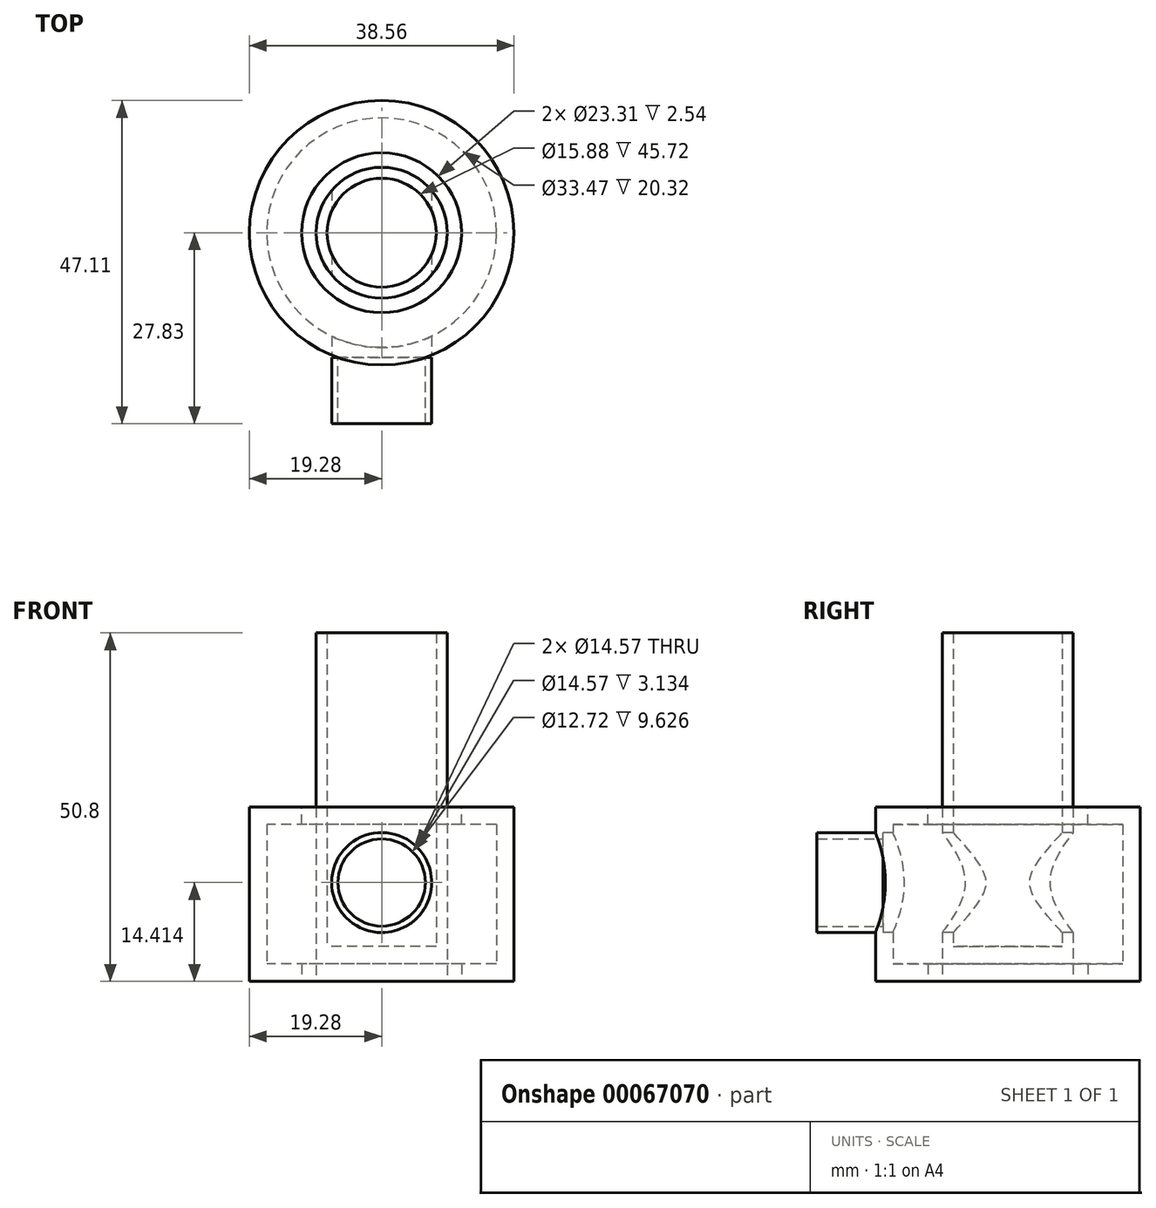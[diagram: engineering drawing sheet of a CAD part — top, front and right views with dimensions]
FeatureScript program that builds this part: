
annotation { "Feature Type Name" : "Feature", "Feature Type Description" : "" }
export const myFeature = defineFeature(function(context is Context, id is Id, definition is map)
    precondition{}
    {
        {
            var Q0;
            Q0=qCreatedBy(makeId("Top.planeOp"),FACE);
            var sketch = newSketch(context, id + "F0", { "sketchPlane" : qUnion([Q0])});
            skCircle(sketch, "E0", {"center": v(0, 0) * mm, "radius": 16.74 * mm});
            skCircle(sketch, "E1", {"center": v(0, 0) * mm, "radius": 11.66 * mm});
            skCircle(sketch, "E2", {"center": v(0, 0) * mm, "radius": 9.54 * mm});
            skCircle(sketch, "E3.0", {"center": v(0, 0) * mm, "radius": 19.28 * mm});
            skCircle(sketch, "E4", {"center": v(0, 0) * mm, "radius": 7.94 * mm});
            skSolve(sketch);
        }
        {
            var Q0;
            Q0=makeQuery(id+"F0.imprint","IMPRINT",FACE,{"disambiguationData":[TD([[makeQuery(id+"F0.imprint","IMPRINT",EDGE,{"derivedFrom":sQuery(id+"F0.wireOp",EDGE,"E0")}),1.0]])]});
            extrude(context, id + "F1", {"entities" : qUnion([Q0]), "depth" : 2.54 * mm});
        }
        {
            var Q0;
            Q0 = qSketchRegion(id + "F0", true);
            extrude(context, id + "F2", {"entities" : qUnion([Q0]), "operationType" : NewBodyOperationType.ADD, "depth" : 25.4 * mm});
        }
        {
            var Q0;
            Q0=makeQuery(id+"F0.imprint","IMPRINT",FACE,{"disambiguationData":[TD([[makeQuery(id+"F0.imprint","IMPRINT",EDGE,{"derivedFrom":sQuery(id+"F0.wireOp",EDGE,"E2")}),1.0]])]});
            extrude(context, id + "F3", {"entities" : qUnion([Q0]), "depth" : 50.8 * mm});
        }
        {
            var Q0;
            Q0=qCreatedBy(makeId("Front.planeOp"),FACE);
            var sketch = newSketch(context, id + "F4", { "sketchPlane" : qUnion([Q0])});
            skCircle(sketch, "E5", {"center": v(0, 14.41) * mm, "radius": 7.29 * mm});
            skSolve(sketch);
        }
        {
            var Q0;
            Q0 = qSketchRegion(id + "F4", true);
            extrude(context, id + "F5", {"entities" : qUnion([Q0]), "operationType" : NewBodyOperationType.REMOVE, "oppositeDirection" : true, "depth" : 11.8 * mm, "hasSecondDirection" : true, "secondDirectionOppositeDirection" : false, "secondDirectionDepth" : 25.05 * mm});
        }
        {
            var Q0;
            Q0=makeQuery(id+"F0.imprint","IMPRINT",FACE,{"disambiguationData":[TD([[makeQuery(id+"F0.imprint","IMPRINT",EDGE,{"derivedFrom":sQuery(id+"F0.wireOp",EDGE,"E4")}),1.0]])]});
            extrude(context, id + "F6", {"entities" : qUnion([Q0]), "operationType" : NewBodyOperationType.ADD, "depth" : 5.08 * mm});
        }
        {
            var Q0;
            Q0=makeQuery(id+"F2.opExtrude","CAP_FACE",FACE,{"disambiguationData":[OSD([sQuery(id+"F0.wireOp",EDGE,"E0"),sQuery(id+"F0.wireOp",EDGE,"E3.0")])],"isStart":false});
            var sketch = newSketch(context, id + "F7", { "sketchPlane" : qUnion([Q0])});
            skCircle(sketch, "E6", {"center": v(0, 0) * mm, "radius": 11.66 * mm});
            skSolve(sketch);
        }
        {
            var Q0;
            Q0=makeQuery(id+"F7.imprint","IMPRINT",FACE,{"disambiguationData":[TD([[makeQuery(id+"F7.imprint","IMPRINT",EDGE,{"derivedFrom":sQuery(id+"F7.wireOp",EDGE,"E6")}),-1.0]])]});
            extrude(context, id + "F8", {"entities" : qUnion([Q0]), "operationType" : NewBodyOperationType.ADD, "oppositeDirection" : true, "depth" : 2.54 * mm});
        }
        {
            var Q0;
            Q0=qCreatedBy(makeId("Front.planeOp"),FACE);
            var sketch = newSketch(context, id + "F9", { "sketchPlane" : qUnion([Q0])});
            skCircle(sketch, "E7", {"center": v(0, 14.41) * mm, "radius": 7.29 * mm});
            skCircle(sketch, "E8", {"center": v(0, 14.41) * mm, "radius": 6.36 * mm});
            skSolve(sketch);
        }
        {
            var Q0;
            Q0=makeQuery(id+"F9.imprint","IMPRINT",FACE,{"disambiguationData":[TD([[makeQuery(id+"F9.imprint","IMPRINT",EDGE,{"derivedFrom":sQuery(id+"F9.wireOp",EDGE,"E7")}),1.0]])]});
            extrude(context, id + "F10", {"entities" : qUnion([Q0]), "operationType" : NewBodyOperationType.ADD, "depth" : 27.83 * mm, "hasSecondDirection" : true, "secondDirectionOppositeDirection" : false, "secondDirectionDepth" : 18.2 * mm});
        }
        {
            var Q0;
            Q0=sQuery(id+"F9.wireOp",VERTEX,"E7.center");
            var Q1;
            Q1=makeQuery(id+"F1.opExtrude","SWEPT_BODY",BODY,{"disambiguationData":[OSD([sQuery(id+"F0.wireOp",EDGE,"E0"),sQuery(id+"F0.wireOp",EDGE,"E1")])]});
            hole(context, id + "F11", {"style" : HoleStyle.SIMPLE, "holeDiameter" : 10.16 * mm, "endStyle" : HoleEndStyle.THROUGH, "oppositeDirection" : true, "locations" : qUnion([Q0]), "scope" : qUnion([Q1])});
        }
        {
            var Q0;
            {var subQ0=sQuery(id+"F0.wireOp",EDGE,"E4");Q0=makeQuery(id+"F6.boolean.opBoolean","MERGE",FACE,{"derivedFrom":[makeQuery(id+"F3.opExtrude","CAP_FACE",FACE,{"disambiguationData":[OSD([sQuery(id+"F0.wireOp",EDGE,"E2"),subQ0])],"isStart":true}),makeQuery(id+"F6.opExtrude","CAP_FACE",FACE,{"disambiguationData":[OSD([subQ0])],"isStart":true})]});}
            cPlane(context, id + "F12", {"entities" : qUnion([Q0]), "cplaneType" : CPlaneType.OFFSET, "offset" : 5.08 * mm, "width" : 152.4 * mm, "height" : 152.4 * mm});
        }
    });
